# Revit family: Door_Coiling_UltiGroup_Komby Value
name_source: partatom
category: Doors
revit_build: Autodesk Revit 2018 (Build: 20170223_1515(x64)
units: mm (PartAtom-declared; Revit-internal decimal feet)

## family parameters
Always vertical = Yes
Cut with Voids When Loaded = No
Host = Wall
OmniClass Number = 23.30.10.00
OmniClass Title = Doors
Room Calculation Point = No
Shared = No

## types (1)
- Type 1
    Aluminium Material = Ulti_Group_Aluminium_Material
    Analytic Construction = <None>
    Control Box Material = Ulti_Group_Control_Box_Material
    Control box height = 1200 mm  [stored 3.93701 ft]
    Description = Ulti Komby Value Roller Shutter and High Speed Door Combination
    DoorFrameFinish_ANZRS = Painted Option RAL colours
    DoorFrameMaterial_ANZRS = Ulti_Group_Roller_Shutter_Door_Frame_Material
    DoorFrameType_ANZRS = Galvanized steel frame
    DoorGlazingHeight_ANZRS = 0 mm  [stored 0 ft]
    DoorGlazingWidth_ANZRS = 0 mm  [stored 0 ft]
    DoorGrilleHeight_ANZRS = 0 mm  [stored 0 ft]
    DoorGrilleWidth_ANZRS = 0 mm  [stored 0 ft]
    DoorGrille_ANZRS = Yes
    DoorNumberOfPanels_ANZRS = 0
    DoorOperation_ANZRS = [OPEN-CLOSE push button][Pneumatically activated with Safety Edge][Manual opening by means of counter weight]
    DoorPanelBWidth_ANZRS = 0 mm  [stored 0 ft]
    DoorPanelDepth_ANZRS = 0 mm  [stored 0 ft]
    DoorPanelHeight_ANZRS = 3700 mm  [stored 12.1391 ft]
    DoorPanelMaterial_ANZRS = Ulti_Group_Roller_Shutter_Door_Panel
    DoorPanelWidth_ANZRS = 0 mm  [stored 0 ft]
    Fax = 07 846 2467
    Function = Interior
    Galvanised Steel = Galvanised Steel
    Height = 3000 mm  [stored 9.84252 ft]
    InstallationGroup_ANZRS = 0
    Manufacturer = Ulti Group Ltd.
    Model = Ulti Komby Value
    ModifiedIssue_ANZRS = 0 $
    Motor colour = Ulti_Group_Motor_Colour
    Number of brackets = 7
    Roller Shutter door panel width = 3100 mm  [stored 10.1706 ft]
    Roller Shutter headroom = 900 mm  [stored 2.95276 ft]
    Roller Shutter open height = 0 mm  [stored 0 ft]
    Rubber Black = Ulti_Group_Rubber_Black_Material
    Send Message = http://ultigroup.co.nz
    Stainless Steel Material = Satinless Steel Tube
    URL = www.ultigroup.co.nz
    Ulti Roll Door Frame material = Ulti_Group_Roll_Door_Frame_Material
    Ulti Roll Opening height = 0 mm  [stored 0 ft]
    Ulti Roll bottom edge = Ulti_Group_Roll_Door_Bottom_Edge_Material
    Ulti Roll curtain colour = Ulti_Group_Roll_Door_Curtain_Colour
    Ulti Roll curtain width = 3040 mm  [stored 9.97375 ft]
    Ulti Roll headroom = 550 mm
    Ulti Roll hood = 350 mm  [stored 1.14829 ft]
    Ulti Roll hood depth = 350 mm  [stored 1.14829 ft]
    Vision Panel = Ulti_Group_PVC_Vision_Panel
    Vision Panel bottom height = 1285 mm  [stored 4.21588 ft]
    Wall Closure = By host
    Width = 3000 mm  [stored 9.84252 ft]

note: [stored X ft] marks values corroborated as IEEE doubles in the binary element streams (Revit-internal decimal feet)

## geometry (parser evidence)
native form markers: Blend x2, Sweep x28
no freeform markers — native parametric forms only
